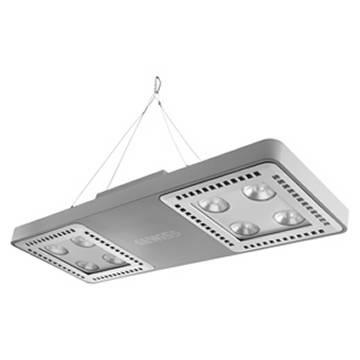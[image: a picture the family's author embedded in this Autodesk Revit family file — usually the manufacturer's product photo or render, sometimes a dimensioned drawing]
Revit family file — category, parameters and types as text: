
# Revit family: LigULing-Industriale-GEWISS-SMART[4]UL_APPARECCHI-LED_2M
name_source: partatom
category: Apparecchi per illuminazione
units: mm (PartAtom-declared; Revit-internal decimal feet)

## family parameters
Basato su piano di lavoro = Sì
Condiviso = No
Numero OmniClass = 23.80.70.00
Punto di calcolo locali = No
Quota connettore circolare = Usa diametro
Sempre verticale = No
Sorgente d'illuminazione = No
Taglio con vuoti quando caricato = No
Tipo di parte = Normale
Titolo OmniClass = Lighting

## types (1)
- LigULing-Industriale-GEWISS-SMART[4]UL_APPARECCHI-LED_2M
    Alimentatore = Incluso
    Apparecchio a ridotta temperatura superficiale = Si
    Applicazione = Interno
    Cablaggio = Cablaggio singolo con cavo antirespirazione che esce da PG metallico (NO Connettore)
    Caratteristiche elettriche e gestione della luce = -
    Caratteristiche ottiche e illuminotecniche = -
    Carico apparente = 97 VA
    Catalogo = LIGHTING
    Certificazione DIN 18032-3 = -
    Certificazioni e classificazioni = -
    Classe fotobiologica = RG0
    Classe isolamento = I
    Classificazione = Lighting
    Classificazione: = -
    Codice Electrocod = 2444
    Codice digitale univoco (Datamatrix) = Datamatrix
    Colore = Grigio RAL 7035
    Commenti sul wattaggio = 97W
    Contesto = Illuminazione di logistiche e locali produttivi industriali
    Controllo abbagliamento e luminanza = UGR - 25
    Corpo = PA6 “Halogen Free” caricato fibra vetro
    Descrizione = SMART[4]HB 2M ST.AL.ON/OFF UL 90° 57K
    Dispositivo di protezione = DM 6 kV / CM 10 kV
    Dist_sorg_lum = 10 mm  [stored 0.0328084 ft]
    Durata di vita = L90B10 (Tq+25°C) = 100.000 h - L90B10 (Tq+40°C) = 50.000 h
    Efficienza luminosa (lm/W) = 138
    Finitura colore = Grigio RAL 7035
    Fissaggio = -
    Frequenza nominale (Hz) = 50/60 Hz
    Gancio di chiusura = -
    Garanzia = 5 anni
    Grado di protezione = IP66
    Gruppo ottico = Riflettore in PC metallizzato e lenti in PMMA
    Guarnizioni = tipo siliconico antinvecchiamento
    IDF = e8aec9e3-8d40-4a75-89d3-d18f5753bf02
    IDT = 05376d21caf540b985b33c65cc7972c3
    IPEA = -
    Immagine tipo = GWL1311.jpg
    Inclinazione = Con accessorio staffa
    Indice di resa cromatica = CRI-80
    Informazioni generali = -
    Installazione e manutenzione = -
    Lampada = LED
    Larghezza = 254 mm
    Lumen output (lm) = 17800
    Lunghezza = 699 mm  [stored 2.29331 ft]
    Mascherina = <Per categoria>
    Materiali = -
    Modello = GWS4220GP857
    Motore = <Per categoria>
    Norma di riferimento = UL 1598 - CSA C22.2 No. 250.0-18
    Ottica = 90°
    Peso (kg): = 6,5
    Potenza di sistema = 129W
    Produttore = GEWISS S.p.A.
    Prospetto di default = 1219 mm
    Resistenza agli urti = IK08
    Resistenza al filo incandescente = 850 °C
    Scheda Tecnica = https://www.gewiss.com
    Schermo = Vetro Temprato Spessore 4mm
    Sistema di controllo = ON / OFF
    Sistema di controllo : = ON / OFF
    Sostituibilità gruppo ottico = Non sostituibile
    Sostituibilità piastra di cablaggio = Non sostituibile
    Spessore plafoniera = 40 mm
    Struttura plafoniera = <Per categoria>
    Superficie massima esposta al vento : = 0,184 m²
    Temperatura di colore = 5700K
    Temperatura di esercizio = -25°C / +40 °C
    Temperatura di stoccaggio = -
    Tensione di alimentazione = 120-277 V
    Tipo di apparecchio = Riflettore industriale a LED&nbsp;
    Tipo di installazione e montaggio = Plafone - Parete - Sospensione
    Tipologia sorgente luminosa = LED - Non sostituibile
    Tolleranza cromatica = SDCM = 3
    Trasformatore = <Per categoria>
    URL = https://www.gewiss.com
    Vano di alimentazione = Integrato
    Versione file RFA = 20.11
    Viti esterne = Acciaio inox
    Voltaggio = 230 V

note: [stored X ft] marks values corroborated as IEEE doubles in the binary element streams (Revit-internal decimal feet)

## geometry (parser evidence)
native form markers: Blend x4, Sweep x3
no freeform markers — native parametric forms only
